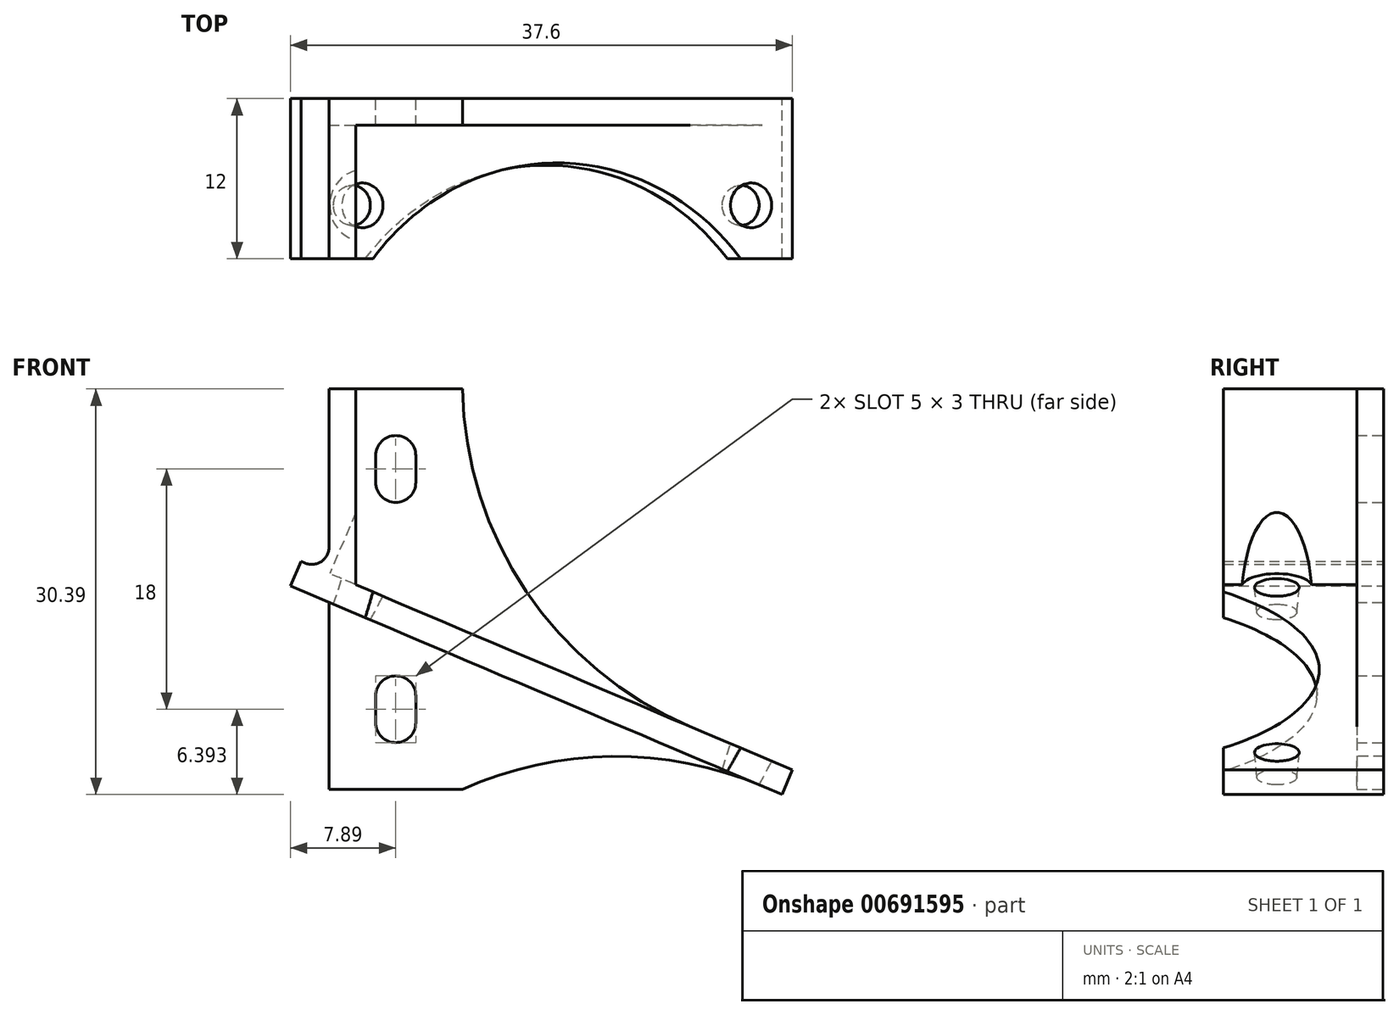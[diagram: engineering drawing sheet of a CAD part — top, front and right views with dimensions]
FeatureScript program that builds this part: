
annotation { "Feature Type Name" : "Feature", "Feature Type Description" : "" }
export const myFeature = defineFeature(function(context is Context, id is Id, definition is map)
    precondition{}
    {
        {
            var Q0;
            Q0=qCreatedBy(makeId("Front.planeOp"),FACE);
            var sketch = newSketch(context, id + "F0", { "sketchPlane" : qUnion([Q0])});
            skCircle(sketch, "E0", {"center": v(0, 14.71) * mm, "radius": 1.5 * mm});
            skCircle(sketch, "E1", {"center": v(0, -3.29) * mm, "radius": 1.5 * mm});
            skCircle(sketch, "E2", {"center": v(0, 12.71) * mm, "radius": 1.5 * mm});
            skLineSegment(sketch, "E3", {"start": v(-1.5, 14.71) * mm, "end": v(-1.5, 12.71) * mm});
            skLineSegment(sketch, "E4", {"start": v(1.5, 14.71) * mm, "end": v(1.5, 12.71) * mm});
            skCircle(sketch, "E5", {"center": v(0, -5.29) * mm, "radius": 1.5 * mm});
            skLineSegment(sketch, "E6", {"start": v(-1.5, -3.29) * mm, "end": v(-1.5, -5.29) * mm});
            skLineSegment(sketch, "E7", {"start": v(1.5, -3.29) * mm, "end": v(1.5, -5.29) * mm});
            skLineSegment(sketch, "E8.bottom", {"start": v(-5, 19.71) * mm, "end": v(5, 19.71) * mm});
            skLineSegment(sketch, "E8.top", {"start": v(-5, -10.29) * mm, "end": v(5, -10.29) * mm});
            skLineSegment(sketch, "E8.left", {"start": v(-5, 19.71) * mm, "end": v(-5, -10.29) * mm});
            skLineSegment(sketch, "E8.right", {"start": v(5, 19.71) * mm, "end": v(5, -10.29) * mm});
            skSolve(sketch);
        }
        {
            var Q0;
            Q0=qSketchRegion(id+"F0",true);
            extrude(context, id + "F1", {"entities" : qUnion([Q0]), "depth" : 2 * mm, "offsetDistance" : 25 * mm});
        }
        {
            var Q0;
            Q0=makeQuery(id+"F1.opExtrude","CAP_FACE",FACE,{"disambiguationData":[OSD([sQuery(id+"F0.wireOp",EDGE,"E0"),sQuery(id+"F0.wireOp",EDGE,"E1"),sQuery(id+"F0.wireOp",EDGE,"E2"),sQuery(id+"F0.wireOp",EDGE,"E3"),sQuery(id+"F0.wireOp",EDGE,"E4"),sQuery(id+"F0.wireOp",EDGE,"E5"),sQuery(id+"F0.wireOp",EDGE,"E6"),sQuery(id+"F0.wireOp",EDGE,"E7"),sQuery(id+"F0.wireOp",EDGE,"E8.bottom"),sQuery(id+"F0.wireOp",EDGE,"E8.top"),sQuery(id+"F0.wireOp",EDGE,"E8.left"),sQuery(id+"F0.wireOp",EDGE,"E8.right")])],"isStart":false});
            var sketch = newSketch(context, id + "F2", { "sketchPlane" : qUnion([Q0])});
            skLineSegment(sketch, "E9", {"start": v(28.93, -10.68) * mm, "end": v(-7.89, 4.95) * mm});
            skLineSegment(sketch, "E10", {"start": v(-7.89, 4.95) * mm, "end": v(-7.1, 6.8) * mm});
            skLineSegment(sketch, "E11", {"start": v(-7.1, 6.8) * mm, "end": v(-6.8, 6.66) * mm});
            skLineSegment(sketch, "E12", {"start": v(29.71, -8.84) * mm, "end": v(28.93, -10.68) * mm});
            skLineSegment(sketch, "E13", {"start": v(-5, 7.86) * mm, "end": v(-5, 19.71) * mm});
            skLineSegment(sketch, "E14", {"start": v(-5, 19.71) * mm, "end": v(-3, 19.71) * mm});
            skLineSegment(sketch, "E15", {"start": v(-3, 19.71) * mm, "end": v(-3, 5.05) * mm});
            skArc(sketch, "E16.filletArc", {"start": v(-6.8, 6.66) * mm, "mid": v(-5.58, 6.78) * mm, "end": v(-5, 7.86) * mm});
            skLineSegment(sketch, "E17", {"start": v(-3, 5.05) * mm, "end": v(29.71, -8.84) * mm});
            skSolve(sketch);
        }
        {
            var Q0;
            {var subQ0=sQuery(id+"F2.wireOp",EDGE,"E10");Q0=makeQuery(id+"F2.imprint","IMPRINT",FACE,{"disambiguationData":[TD([[makeQuery(id+"F2.imprint","IMPRINT",EDGE,{"derivedFrom":subQ0}),-1.0]])]});}
            var Q1;
            {var subQ0=sQuery(id+"F2.wireOp",EDGE,"E12");Q1=makeQuery(id+"F2.imprint","IMPRINT",FACE,{"disambiguationData":[TD([[makeQuery(id+"F2.imprint","IMPRINT",EDGE,{"derivedFrom":subQ0}),-1.0]])]});}
            var Q2;
            {var subQ0=sQuery(id+"F2.wireOp",EDGE,"SCbIJ3P8-rOfK-h0km-0NJx-cdtD0Zfjy0IP");Q2=makeQuery(id+"F2.imprint","IMPRINT",FACE,{"disambiguationData":[TD([[makeQuery(id+"F2.imprint","IMPRINT",EDGE,{"derivedFrom":subQ0}),-1.0]])]});}
            var Q3;
            {var subQ0=sQuery(id+"F2.wireOp",EDGE,"E13");Q3=makeQuery(id+"F2.imprint","IMPRINT",FACE,{"disambiguationData":[TD([[makeQuery(id+"F2.imprint","IMPRINT",EDGE,{"derivedFrom":subQ0}),1.0]])]});}
            var Q4;
            Q4=makeQuery(id+"F1.opExtrude","CAP_FACE",FACE,{"disambiguationData":[OSD([sQuery(id+"F0.wireOp",EDGE,"E0"),sQuery(id+"F0.wireOp",EDGE,"E1"),sQuery(id+"F0.wireOp",EDGE,"E2"),sQuery(id+"F0.wireOp",EDGE,"E3"),sQuery(id+"F0.wireOp",EDGE,"E4"),sQuery(id+"F0.wireOp",EDGE,"E5"),sQuery(id+"F0.wireOp",EDGE,"E6"),sQuery(id+"F0.wireOp",EDGE,"E7"),sQuery(id+"F0.wireOp",EDGE,"E8.bottom"),sQuery(id+"F0.wireOp",EDGE,"E8.top"),sQuery(id+"F0.wireOp",EDGE,"E8.left"),sQuery(id+"F0.wireOp",EDGE,"E8.right")])],"isStart":true});
            extrude(context, id + "F3", {"entities" : qUnion([Q0, Q1, Q2, Q3]), "operationType" : NewBodyOperationType.ADD, "depth" : 10 * mm, "offsetDistance" : 25 * mm, "hasSecondDirection" : true, "secondDirectionBound" : SecondDirectionBoundingType.UP_TO_SURFACE, "secondDirectionOppositeDirection" : true, "secondDirectionDepth" : 25 * mm, "secondDirectionBoundEntityFace" : qUnion([Q4])});
        }
        {
            var Q0;
            Q0=makeQuery(id+"F3.opExtrude","SWEPT_FACE",FACE,{"disambiguationData":[OSD([sQuery(id+"F2.wireOp",EDGE,"E9")])]});
            var sketch = newSketch(context, id + "F4", { "sketchPlane" : qUnion([Q0])});
            skCircle(sketch, "E18", {"center": v(-4.2, 8) * mm, "radius": 1.5 * mm});
            skCircle(sketch, "E19", {"center": v(27.44, 8) * mm, "radius": 1.5 * mm});
            skCircle(sketch, "E20", {"center": v(11.63, 24) * mm, "radius": 19 * mm});
            skSolve(sketch);
        }
        {
            var Q0;
            Q0=qSketchRegion(id+"F4",true);
            var Q1;
            Q1=makeQuery(id+"F3.opExtrude","SWEPT_FACE",FACE,{"disambiguationData":[OSD([sQuery(id+"F2.wireOp",EDGE,"E11")])]});
            extrude(context, id + "F5", {"entities" : qUnion([Q0]), "operationType" : NewBodyOperationType.REMOVE, "endBound" : BoundingType.THROUGH_ALL, "oppositeDirection" : true, "depth" : 25 * mm, "endBoundEntityFace" : qUnion([Q1]), "offsetDistance" : 25 * mm, "hasDraft" : true, "draftAngle" : 5 * degree});
        }
        {
            var Q0;
            {var subQ1=sQuery(id+"F2.wireOp",EDGE,"E17");Q0=makeQuery(id+"F5.boolean.opBoolean","SPLIT",FACE,{"disambiguationData":[TD([makeQuery(id+"F5.opExtrude","SWEPT_FACE",FACE,{"disambiguationData":[OSD([sQuery(id+"F4.wireOp",EDGE,"E19")])]})])],"derivedFrom":makeQuery(id+"F3.opExtrude","SWEPT_FACE",FACE,{"disambiguationData":[OSD([subQ1])]})});}
            var sketch = newSketch(context, id + "F6", { "sketchPlane" : qUnion([Q0])});
            skCircle(sketch, "E21", {"center": v(27.44, -8) * mm, "radius": 2.65 * mm});
            skArc(sketch, "E22.0", {"start": v(-4.73, -6.41) * mm, "mid": v(-5.87, -8) * mm, "end": v(-4.73, -9.59) * mm});
            skCircle(sketch, "E23", {"center": v(-4.2, -8) * mm, "radius": 2.65 * mm});
            skSolve(sketch);
        }
        {
            var Q0;
            Q0=qSketchRegion(id+"F6",true);
            var Q1;
            Q1=makeQuery(id+"FUSuy9nRfmVc19A_1.boolean.opBoolean","MERGE",FACE,{"derivedFrom":[makeQuery(id+"F3.boolean.opBoolean","MERGE",FACE,{"derivedFrom":[makeQuery(id+"F1.opExtrude","SWEPT_FACE",FACE,{"disambiguationData":[OSD([sQuery(id+"F0.wireOp",EDGE,"E8.bottom")])]}),makeQuery(id+"F3.opExtrude","SWEPT_FACE",FACE,{"disambiguationData":[OSD([sQuery(id+"F2.wireOp",EDGE,"E14")])]})]}),makeQuery(id+"FUSuy9nRfmVc19A_1.opExtrude","SWEPT_FACE",FACE,{"disambiguationData":[OSD([sQuery(id+"F6FWnIPVS1r365c_1.wireOp",EDGE,"eoJ0XLl9-pqLg-lpWe-Bwn1-XGqlSiOjqJmM")])]})]});
            extrude(context, id + "F7", {"entities" : qUnion([Q0]), "operationType" : NewBodyOperationType.REMOVE, "endBound" : BoundingType.UP_TO_SURFACE, "depth" : 25 * mm, "endBoundEntityFace" : qUnion([Q1]), "offsetDistance" : 25 * mm});
        }
        {
            var Q0;
            Q0=makeQuery(id+"F3.boolean.opBoolean","INTERSECT",EDGE,{"derivedFrom":[makeQuery(id+"F1.opExtrude","SWEPT_FACE",FACE,{"disambiguationData":[OSD([sQuery(id+"F0.wireOp",EDGE,"E8.right")])]}),makeQuery(id+"F3.opExtrude","SWEPT_FACE",FACE,{"disambiguationData":[OSD([sQuery(id+"F2.wireOp",EDGE,"E17")])]})]});
            var Q1;
            Q1=makeQuery(id+"F3.boolean.opBoolean","INTERSECT",EDGE,{"derivedFrom":[makeQuery(id+"F1.opExtrude","SWEPT_FACE",FACE,{"disambiguationData":[OSD([sQuery(id+"F0.wireOp",EDGE,"E8.right")])]}),makeQuery(id+"F3.opExtrude","SWEPT_FACE",FACE,{"disambiguationData":[OSD([sQuery(id+"F2.wireOp",EDGE,"E9")])]})]});
            fillet(context, id + "F8", {"entities" : qUnion([Q0, Q1]), "radius" : 28 * mm, "tangentPropagation" : true, "allowEdgeOverflow" : false});
        }
    });
